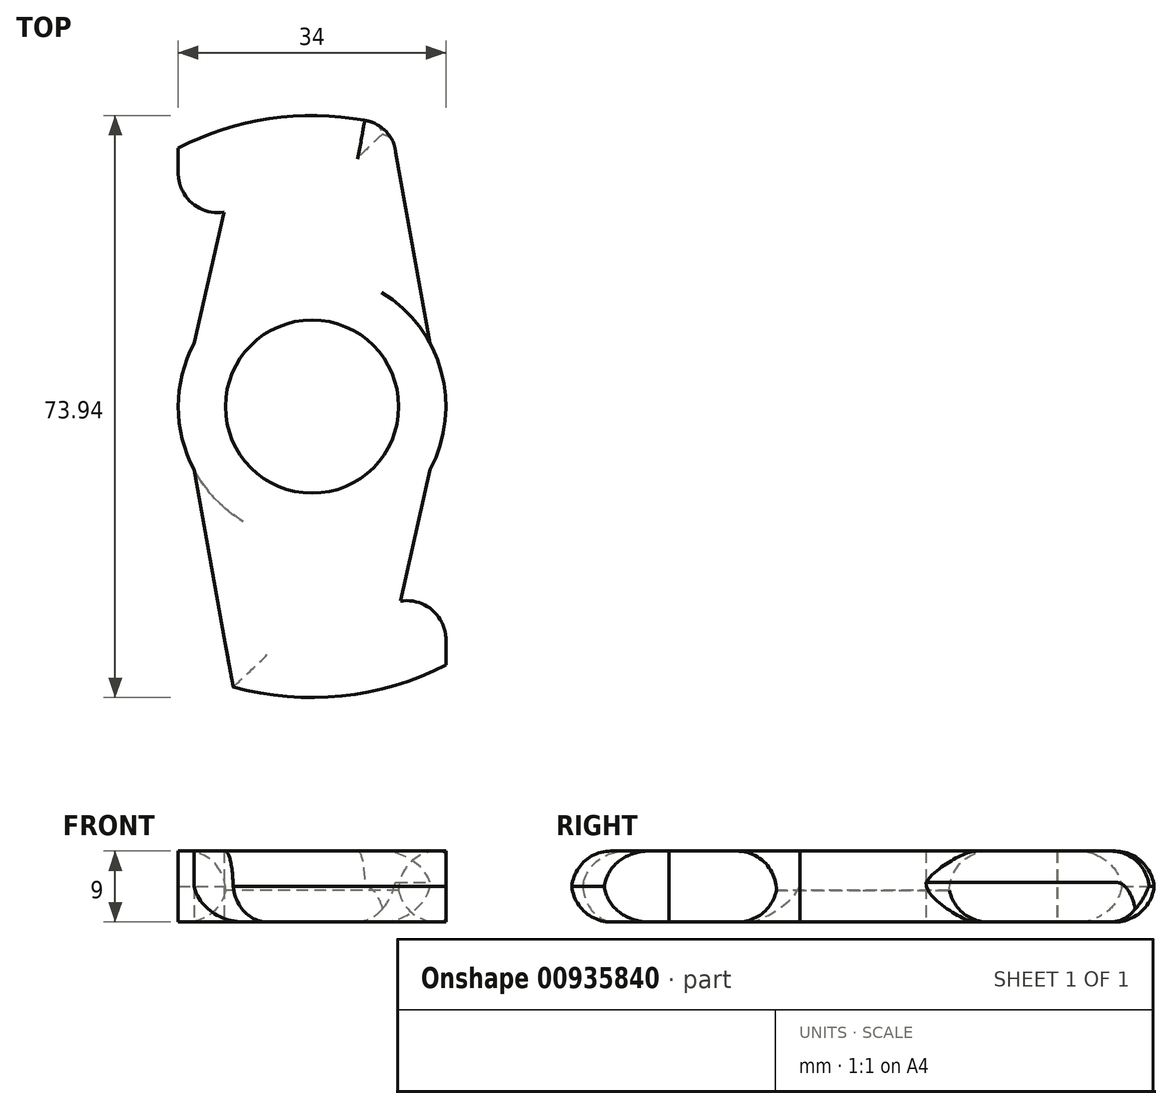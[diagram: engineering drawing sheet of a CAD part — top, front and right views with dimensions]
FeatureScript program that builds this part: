
annotation { "Feature Type Name" : "Feature", "Feature Type Description" : "" }
export const myFeature = defineFeature(function(context is Context, id is Id, definition is map)
    precondition{}
    {
        {
            var Q0;
            Q0=qCreatedBy(makeId("Top.planeOp"),FACE);
            var sketch = newSketch(context, id + "F0", { "sketchPlane" : qUnion([Q0])});
            skCircle(sketch, "E0", {"center": v(0, 0) * mm, "radius": 11 * mm});
            skLineSegment(sketch, "E1", {"start": v(-17, 32.86) * mm, "end": v(-17, 23.16) * mm});
            skLineSegment(sketch, "E2", {"start": v(-17, 23.16) * mm, "end": v(-11.2, 24.71) * mm});
            skLineSegment(sketch, "E3", {"start": v(-11.2, 24.71) * mm, "end": v(-15, 8) * mm});
            skLineSegment(sketch, "E4", {"start": v(10.03, 35.62) * mm, "end": v(15, 8) * mm});
            skLineSegment(sketch, "E5", {"start": v(-15, 8) * mm, "end": v(15, 8) * mm, "construction": true});
            skArc(sketch, "E6", {"start": v(10.03, 35.62) * mm, "mid": v(-3.75, 36.8) * mm, "end": v(-17, 32.86) * mm});
            skArc(sketch, "E7", {"start": v(15, 8) * mm, "mid": v(0, 17) * mm, "end": v(-15, 8) * mm, "construction": true});
            skArc(sketch, "E8", {"start": v(-15, 8) * mm, "mid": v(-16.5, 4.12) * mm, "end": v(-17, 0) * mm});
            skArc(sketch, "E9", {"start": v(17, 0) * mm, "mid": v(16.5, 4.12) * mm, "end": v(15, 8) * mm});
            skArc(sketch, "E10.1.0", {"start": v(15, -8) * mm, "mid": v(16.5, -4.12) * mm, "end": v(17, 0) * mm});
            skLineSegment(sketch, "E10.1.1", {"start": v(11.2, -24.71) * mm, "end": v(15, -8) * mm});
            skArc(sketch, "E10.1.2", {"start": v(-15, -8) * mm, "mid": v(0, -17) * mm, "end": v(15, -8) * mm, "construction": true});
            skLineSegment(sketch, "E10.1.3", {"start": v(15, -8) * mm, "end": v(-15, -8) * mm, "construction": true});
            skLineSegment(sketch, "E10.1.4", {"start": v(17, -23.16) * mm, "end": v(11.2, -24.71) * mm});
            skLineSegment(sketch, "E10.1.5", {"start": v(17, -32.86) * mm, "end": v(17, -23.16) * mm});
            skArc(sketch, "E10.1.6", {"start": v(-10.03, -35.62) * mm, "mid": v(3.75, -36.8) * mm, "end": v(17, -32.86) * mm});
            skLineSegment(sketch, "E10.1.7", {"start": v(-10.03, -35.62) * mm, "end": v(-15, -8) * mm});
            skArc(sketch, "E10.1.8", {"start": v(-17, 0) * mm, "mid": v(-16.5, -4.12) * mm, "end": v(-15, -8) * mm});
            skSolve(sketch);
        }
        {
            var Q0;
            Q0=makeQuery(id+"F0.imprint","IMPRINT",FACE,{"disambiguationData":[TD([[makeQuery(id+"F0.imprint","IMPRINT",EDGE,{"derivedFrom":sQuery(id+"F0.wireOp",EDGE,"E0")}),-1.0]])]});
            extrude(context, id + "F1", {"entities" : qUnion([Q0]), "depth" : 9 * mm, "offsetDistance" : 25 * mm});
        }
        {
            var Q0;
            Q0=makeQuery(id+"F1.opExtrude","CAP_EDGE",EDGE,{"disambiguationData":[OSD([sQuery(id+"F0.wireOp",EDGE,"E0")])],"isStart":false});
            var Q1;
            Q1=makeQuery(id+"F1.opExtrude","CAP_EDGE",EDGE,{"disambiguationData":[OSD([sQuery(id+"F0.wireOp",EDGE,"E10.1.6")])],"isStart":false});
            var Q2;
            Q2=makeQuery(id+"F1.opExtrude","CAP_EDGE",EDGE,{"disambiguationData":[OSD([sQuery(id+"F0.wireOp",EDGE,"E10.1.6")])],"isStart":true});
            var Q3;
            Q3=makeQuery(id+"F1.opExtrude","CAP_EDGE",EDGE,{"disambiguationData":[OSD([sQuery(id+"F0.wireOp",EDGE,"E6")])],"isStart":false});
            var Q4;
            Q4=makeQuery(id+"F1.opExtrude","CAP_EDGE",EDGE,{"disambiguationData":[OSD([sQuery(id+"F0.wireOp",EDGE,"E6")])],"isStart":true});
            fillet(context, id + "F2", {"entities" : qUnion([Q0, Q1, Q2, Q3, Q4]), "radius" : 5 * mm, "tangentPropagation" : true, "allowEdgeOverflow" : false});
        }
        {
            var Q0;
            Q0=makeQuery(id+"F1.opExtrude","CAP_EDGE",EDGE,{"disambiguationData":[OSD([sQuery(id+"F0.wireOp",EDGE,"E0")])],"isStart":true});
            fillet(context, id + "F3", {"entities" : qUnion([Q0]), "radius" : 5 * mm, "tangentPropagation" : true, "allowEdgeOverflow" : false});
        }
        {
            var Q0;
            Q0=makeQuery(id+"F1.opExtrude","SWEPT_EDGE",EDGE,{"disambiguationData":[OSD([sQuery(id+"F0.wireOp",EDGE,"E10.1.4"),sQuery(id+"F0.wireOp",EDGE,"E10.1.5")])]});
            var Q1;
            Q1=makeQuery(id+"F1.opExtrude","SWEPT_EDGE",EDGE,{"disambiguationData":[OSD([sQuery(id+"F0.wireOp",EDGE,"E1"),sQuery(id+"F0.wireOp",EDGE,"E2")])]});
            fillet(context, id + "F4", {"entities" : qUnion([Q0, Q1]), "radius" : 5 * mm, "tangentPropagation" : true, "allowEdgeOverflow" : false});
        }
        {
            var Q0;
            Q0=makeQuery(id+"F1.opExtrude","CAP_EDGE",EDGE,{"disambiguationData":[OSD([sQuery(id+"F0.wireOp",EDGE,"E10.1.7")])],"isStart":true});
            fillet(context, id + "F5", {"entities" : qUnion([Q0]), "radius" : 5 * mm, "tangentPropagation" : true, "allowEdgeOverflow" : false});
        }
        {
            var Q0;
            Q0=makeQuery(id+"F1.opExtrude","CAP_EDGE",EDGE,{"disambiguationData":[OSD([sQuery(id+"F0.wireOp",EDGE,"E4")])],"isStart":true});
            fillet(context, id + "F6", {"entities" : qUnion([Q0]), "radius" : 5 * mm, "tangentPropagation" : true, "allowEdgeOverflow" : false});
        }
        {
            var Q0;
            Q0=makeQuery(id+"F1.opExtrude","CAP_EDGE",EDGE,{"disambiguationData":[OSD([sQuery(id+"F0.wireOp",EDGE,"E4")])],"isStart":false});
            fillet(context, id + "F7", {"entities" : qUnion([Q0]), "radius" : 5 * mm, "tangentPropagation" : true, "allowEdgeOverflow" : false});
        }
    });
